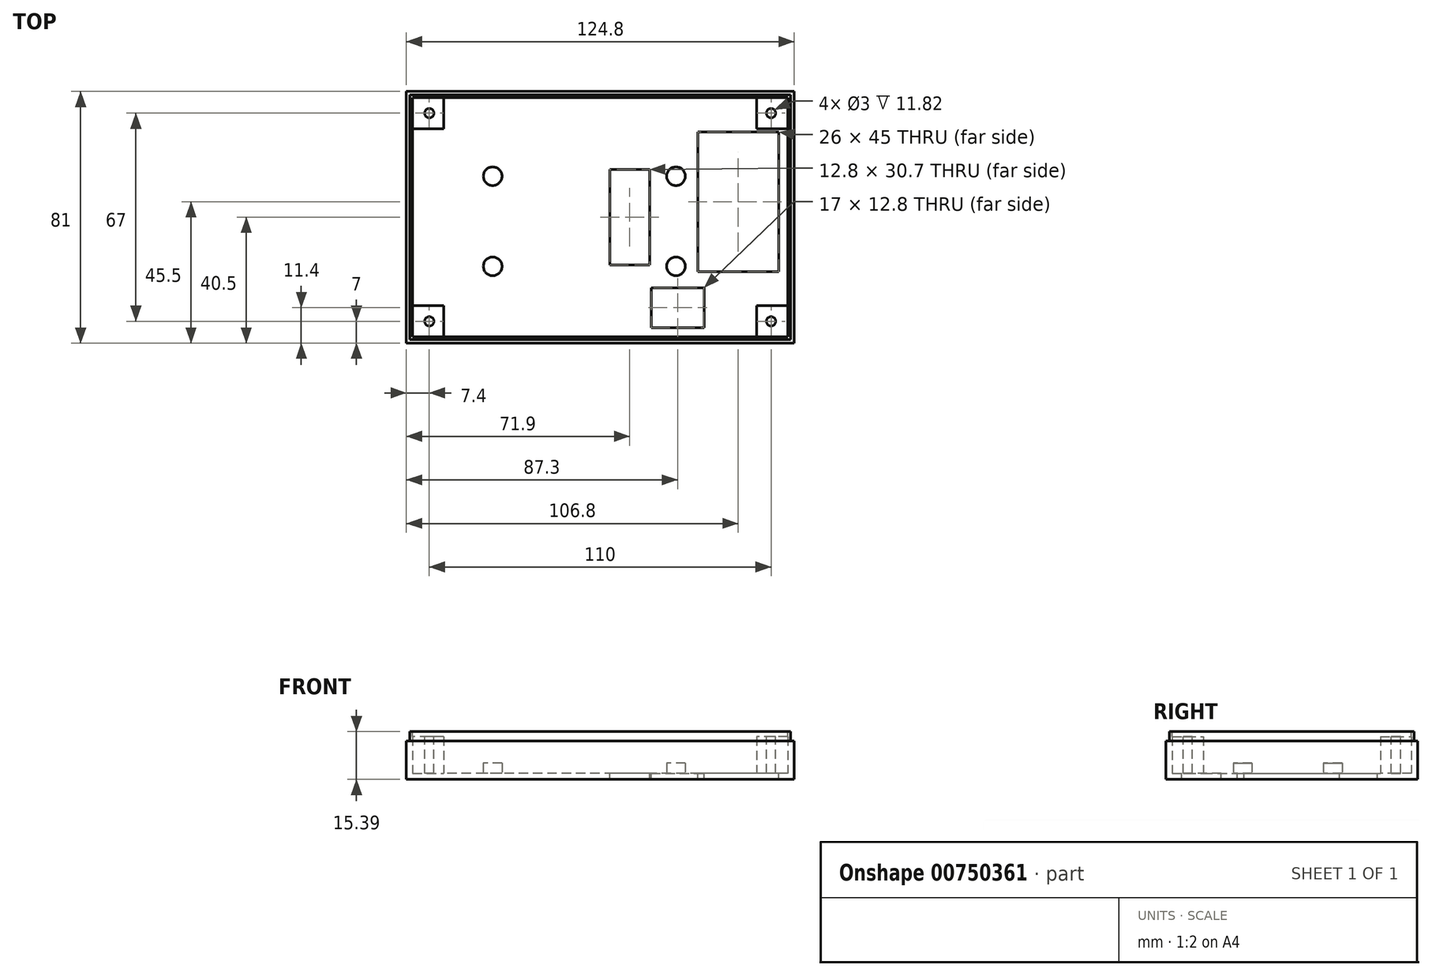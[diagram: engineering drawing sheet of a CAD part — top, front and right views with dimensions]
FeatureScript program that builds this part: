
annotation { "Feature Type Name" : "Feature", "Feature Type Description" : "" }
export const myFeature = defineFeature(function(context is Context, id is Id, definition is map)
    precondition{}
    {
        {
            var Q0;
            Q0=qCreatedBy(makeId("Top.planeOp"),FACE);
            var sketch = newSketch(context, id + "F0", { "sketchPlane" : qUnion([Q0])});
            skLineSegment(sketch, "E0.bottom", {"start": v(-62.4, -40.5) * mm, "end": v(62.4, -40.5) * mm});
            skLineSegment(sketch, "E0.top", {"start": v(-62.4, 40.5) * mm, "end": v(62.4, 40.5) * mm});
            skLineSegment(sketch, "E0.left", {"start": v(-62.4, -40.5) * mm, "end": v(-62.4, 40.5) * mm});
            skLineSegment(sketch, "E0.right", {"start": v(62.4, -40.5) * mm, "end": v(62.4, 40.5) * mm});
            skPoint(sketch, "E0.middle", {"position": v(0, 0) * mm});
            skSolve(sketch);
        }
        {
            var Q0;
            Q0=makeQuery(id+"F0.imprint","IMPRINT",FACE,{"disambiguationData":[TD([[makeQuery(id+"F0.imprint","IMPRINT",EDGE,{"derivedFrom":sQuery(id+"F0.wireOp",EDGE,"E0.bottom")}),1.0]])]});
            extrude(context, id + "F1", {"entities" : qUnion([Q0]), "depth" : 15.4 * mm, "offsetDistance" : 25 * mm});
        }
        {
            var Q0;
            Q0=makeQuery(id+"F1.opExtrude","CAP_FACE",FACE,{"disambiguationData":[OSD([sQuery(id+"F0.wireOp",EDGE,"E0.bottom"),sQuery(id+"F0.wireOp",EDGE,"E0.top"),sQuery(id+"F0.wireOp",EDGE,"E0.left"),sQuery(id+"F0.wireOp",EDGE,"E0.right")])],"isStart":false});
            var sketch = newSketch(context, id + "F2", { "sketchPlane" : qUnion([Q0])});
            skLineSegment(sketch, "E1.bottom", {"start": v(60.4, -38.5) * mm, "end": v(-60.4, -38.5) * mm});
            skLineSegment(sketch, "E1.top", {"start": v(60.4, 38.5) * mm, "end": v(-60.4, 38.5) * mm});
            skLineSegment(sketch, "E1.left", {"start": v(60.4, -38.5) * mm, "end": v(60.4, 38.5) * mm});
            skLineSegment(sketch, "E1.right", {"start": v(-60.4, -38.5) * mm, "end": v(-60.4, 38.5) * mm});
            skPoint(sketch, "E1.middle", {"position": v(0, 0) * mm});
            skSolve(sketch);
        }
        {
            var Q0;
            Q0=makeQuery(id+"F2.imprint","IMPRINT",FACE,{"disambiguationData":[TD([[makeQuery(id+"F2.imprint","IMPRINT",EDGE,{"derivedFrom":sQuery(id+"F2.wireOp",EDGE,"E1.bottom")}),-1.0]])]});
            extrude(context, id + "F3", {"entities" : qUnion([Q0]), "operationType" : NewBodyOperationType.REMOVE, "oppositeDirection" : true, "depth" : 13.4 * mm, "offsetDistance" : 25 * mm});
        }
        {
            var Q0;
            Q0=makeQuery(id+"F1.opExtrude","SWEPT_FACE",FACE,{"disambiguationData":[OSD([sQuery(id+"F0.wireOp",EDGE,"E0.top")])]});
            var sketch = newSketch(context, id + "F4", { "sketchPlane" : qUnion([Q0])});
            skLineSegment(sketch, "E2.bottom", {"start": v(-62.4, 15.4) * mm, "end": v(62.4, 15.4) * mm});
            skLineSegment(sketch, "E2.top", {"start": v(-62.4, 12.4) * mm, "end": v(62.4, 12.4) * mm});
            skLineSegment(sketch, "E2.left", {"start": v(-62.4, 15.4) * mm, "end": v(-62.4, 12.4) * mm});
            skLineSegment(sketch, "E2.right", {"start": v(62.4, 15.4) * mm, "end": v(62.4, 12.4) * mm});
            skSolve(sketch);
        }
        {
            var Q0;
            Q0=makeQuery(id+"F4.imprint","IMPRINT",FACE,{"disambiguationData":[TD([[makeQuery(id+"F4.imprint","IMPRINT",EDGE,{"derivedFrom":sQuery(id+"F4.wireOp",EDGE,"E2.bottom")}),1.0]])]});
            extrude(context, id + "F5", {"entities" : qUnion([Q0]), "operationType" : NewBodyOperationType.REMOVE, "oppositeDirection" : true, "depth" : 1.15 * mm, "offsetDistance" : 25 * mm});
        }
        {
            var Q0;
            Q0=makeQuery(id+"F1.opExtrude","SWEPT_FACE",FACE,{"disambiguationData":[OSD([sQuery(id+"F0.wireOp",EDGE,"E0.bottom")])]});
            var sketch = newSketch(context, id + "F6", { "sketchPlane" : qUnion([Q0])});
            skLineSegment(sketch, "E3.bottom", {"start": v(-62.4, 15.4) * mm, "end": v(62.4, 15.4) * mm});
            skLineSegment(sketch, "E3.top", {"start": v(-62.4, 12.4) * mm, "end": v(62.4, 12.4) * mm});
            skLineSegment(sketch, "E3.left", {"start": v(-62.4, 15.4) * mm, "end": v(-62.4, 12.4) * mm});
            skLineSegment(sketch, "E3.right", {"start": v(62.4, 15.4) * mm, "end": v(62.4, 12.4) * mm});
            skSolve(sketch);
        }
        {
            var Q0;
            Q0=makeQuery(id+"F6.imprint","IMPRINT",FACE,{"disambiguationData":[TD([[makeQuery(id+"F6.imprint","IMPRINT",EDGE,{"derivedFrom":sQuery(id+"F6.wireOp",EDGE,"E3.bottom")}),-1.0]])]});
            extrude(context, id + "F7", {"entities" : qUnion([Q0]), "operationType" : NewBodyOperationType.REMOVE, "oppositeDirection" : true, "depth" : 1.15 * mm, "offsetDistance" : 25 * mm});
        }
        {
            var Q0;
            Q0=makeQuery(id+"F1.opExtrude","SWEPT_FACE",FACE,{"disambiguationData":[OSD([sQuery(id+"F0.wireOp",EDGE,"E0.right")])]});
            var sketch = newSketch(context, id + "F8", { "sketchPlane" : qUnion([Q0])});
            skLineSegment(sketch, "E4.bottom", {"start": v(-39.35, 15.4) * mm, "end": v(39.35, 15.4) * mm});
            skLineSegment(sketch, "E4.top", {"start": v(-39.35, 12.4) * mm, "end": v(39.35, 12.4) * mm});
            skLineSegment(sketch, "E4.left", {"start": v(-39.35, 15.4) * mm, "end": v(-39.35, 12.4) * mm});
            skLineSegment(sketch, "E4.right", {"start": v(39.35, 15.4) * mm, "end": v(39.35, 12.4) * mm});
            skSolve(sketch);
        }
        {
            var Q0;
            Q0=makeQuery(id+"F8.imprint","IMPRINT",FACE,{"disambiguationData":[TD([[makeQuery(id+"F8.imprint","IMPRINT",EDGE,{"derivedFrom":sQuery(id+"F8.wireOp",EDGE,"E4.bottom")}),-1.0]])]});
            extrude(context, id + "F9", {"entities" : qUnion([Q0]), "operationType" : NewBodyOperationType.REMOVE, "oppositeDirection" : true, "depth" : 1.15 * mm, "offsetDistance" : 25 * mm});
        }
        {
            var Q0;
            Q0=makeQuery(id+"F1.opExtrude","SWEPT_FACE",FACE,{"disambiguationData":[OSD([sQuery(id+"F0.wireOp",EDGE,"E0.left")])]});
            var sketch = newSketch(context, id + "F10", { "sketchPlane" : qUnion([Q0])});
            skLineSegment(sketch, "E5.bottom", {"start": v(-39.35, 15.4) * mm, "end": v(39.35, 15.4) * mm});
            skLineSegment(sketch, "E5.top", {"start": v(-39.35, 12.4) * mm, "end": v(39.35, 12.4) * mm});
            skLineSegment(sketch, "E5.left", {"start": v(-39.35, 15.4) * mm, "end": v(-39.35, 12.4) * mm});
            skLineSegment(sketch, "E5.right", {"start": v(39.35, 15.4) * mm, "end": v(39.35, 12.4) * mm});
            skSolve(sketch);
        }
        {
            var Q0;
            Q0=makeQuery(id+"F10.imprint","IMPRINT",FACE,{"disambiguationData":[TD([[makeQuery(id+"F10.imprint","IMPRINT",EDGE,{"derivedFrom":sQuery(id+"F10.wireOp",EDGE,"E5.bottom")}),1.0]])]});
            extrude(context, id + "F11", {"entities" : qUnion([Q0]), "operationType" : NewBodyOperationType.REMOVE, "oppositeDirection" : true, "depth" : 1.15 * mm, "offsetDistance" : 25 * mm});
        }
        {
            var Q0;
            Q0=makeQuery(id+"F3.boolean.opBoolean","COPY",FACE,{"derivedFrom":makeQuery(id+"F3.opExtrude","CAP_FACE",FACE,{"disambiguationData":[OSD([sQuery(id+"F2.wireOp",EDGE,"E1.bottom"),sQuery(id+"F2.wireOp",EDGE,"E1.top"),sQuery(id+"F2.wireOp",EDGE,"E1.left"),sQuery(id+"F2.wireOp",EDGE,"E1.right")])],"isStart":false})});
            var sketch = newSketch(context, id + "F12", { "sketchPlane" : qUnion([Q0])});
            skLineSegment(sketch, "E6.bottom", {"start": v(-60.4, 38.5) * mm, "end": v(-50.4, 38.5) * mm});
            skLineSegment(sketch, "E6.top", {"start": v(-60.4, 28.5) * mm, "end": v(-50.4, 28.5) * mm});
            skLineSegment(sketch, "E6.left", {"start": v(-60.4, 38.5) * mm, "end": v(-60.4, 28.5) * mm});
            skLineSegment(sketch, "E6.right", {"start": v(-50.4, 38.5) * mm, "end": v(-50.4, 28.5) * mm});
            skSolve(sketch);
        }
        {
            var Q0;
            Q0=makeQuery(id+"F12.imprint","IMPRINT",FACE,{"disambiguationData":[TD([[makeQuery(id+"F12.imprint","IMPRINT",EDGE,{"derivedFrom":sQuery(id+"F12.wireOp",EDGE,"E6.bottom")}),1.0]])]});
            extrude(context, id + "F13", {"entities" : qUnion([Q0]), "operationType" : NewBodyOperationType.ADD, "depth" : 11.82 * mm, "offsetDistance" : 25 * mm});
        }
        {
            var Q0;
            Q0=makeQuery(id+"F3.boolean.opBoolean","COPY",FACE,{"derivedFrom":makeQuery(id+"F3.opExtrude","CAP_FACE",FACE,{"disambiguationData":[OSD([sQuery(id+"F2.wireOp",EDGE,"E1.bottom"),sQuery(id+"F2.wireOp",EDGE,"E1.top"),sQuery(id+"F2.wireOp",EDGE,"E1.left"),sQuery(id+"F2.wireOp",EDGE,"E1.right")])],"isStart":false})});
            var sketch = newSketch(context, id + "F14", { "sketchPlane" : qUnion([Q0])});
            skLineSegment(sketch, "E7.bottom", {"start": v(-60.4, -38.5) * mm, "end": v(-50.4, -38.5) * mm});
            skLineSegment(sketch, "E7.top", {"start": v(-60.4, -28.5) * mm, "end": v(-50.4, -28.5) * mm});
            skLineSegment(sketch, "E7.left", {"start": v(-60.4, -38.5) * mm, "end": v(-60.4, -28.5) * mm});
            skLineSegment(sketch, "E7.right", {"start": v(-50.4, -38.5) * mm, "end": v(-50.4, -28.5) * mm});
            skSolve(sketch);
        }
        {
            var Q0;
            Q0=makeQuery(id+"F14.imprint","IMPRINT",FACE,{"disambiguationData":[TD([[makeQuery(id+"F14.imprint","IMPRINT",EDGE,{"derivedFrom":sQuery(id+"F14.wireOp",EDGE,"E7.bottom")}),-1.0]])]});
            extrude(context, id + "F15", {"entities" : qUnion([Q0]), "operationType" : NewBodyOperationType.ADD, "depth" : 11.82 * mm, "offsetDistance" : 25 * mm});
        }
        {
            var Q0;
            Q0=makeQuery(id+"F3.boolean.opBoolean","COPY",FACE,{"derivedFrom":makeQuery(id+"F3.opExtrude","CAP_FACE",FACE,{"disambiguationData":[OSD([sQuery(id+"F2.wireOp",EDGE,"E1.bottom"),sQuery(id+"F2.wireOp",EDGE,"E1.top"),sQuery(id+"F2.wireOp",EDGE,"E1.left"),sQuery(id+"F2.wireOp",EDGE,"E1.right")])],"isStart":false})});
            var sketch = newSketch(context, id + "F16", { "sketchPlane" : qUnion([Q0])});
            skLineSegment(sketch, "E8.bottom", {"start": v(60.4, -38.5) * mm, "end": v(50.4, -38.5) * mm});
            skLineSegment(sketch, "E8.top", {"start": v(60.4, -28.5) * mm, "end": v(50.4, -28.5) * mm});
            skLineSegment(sketch, "E8.left", {"start": v(60.4, -38.5) * mm, "end": v(60.4, -28.5) * mm});
            skLineSegment(sketch, "E8.right", {"start": v(50.4, -38.5) * mm, "end": v(50.4, -28.5) * mm});
            skSolve(sketch);
        }
        {
            var Q0;
            Q0=makeQuery(id+"F16.imprint","IMPRINT",FACE,{"disambiguationData":[TD([[makeQuery(id+"F16.imprint","IMPRINT",EDGE,{"derivedFrom":sQuery(id+"F16.wireOp",EDGE,"E8.bottom")}),-1.0]])]});
            extrude(context, id + "F17", {"entities" : qUnion([Q0]), "operationType" : NewBodyOperationType.ADD, "depth" : 11.82 * mm, "offsetDistance" : 25 * mm});
        }
        {
            var Q0;
            Q0=makeQuery(id+"F3.boolean.opBoolean","COPY",FACE,{"derivedFrom":makeQuery(id+"F3.opExtrude","CAP_FACE",FACE,{"disambiguationData":[OSD([sQuery(id+"F2.wireOp",EDGE,"E1.bottom"),sQuery(id+"F2.wireOp",EDGE,"E1.top"),sQuery(id+"F2.wireOp",EDGE,"E1.left"),sQuery(id+"F2.wireOp",EDGE,"E1.right")])],"isStart":false})});
            var sketch = newSketch(context, id + "F18", { "sketchPlane" : qUnion([Q0])});
            skLineSegment(sketch, "E9.bottom", {"start": v(60.4, 38.5) * mm, "end": v(50.4, 38.5) * mm});
            skLineSegment(sketch, "E9.top", {"start": v(60.4, 28.5) * mm, "end": v(50.4, 28.5) * mm});
            skLineSegment(sketch, "E9.left", {"start": v(60.4, 38.5) * mm, "end": v(60.4, 28.5) * mm});
            skLineSegment(sketch, "E9.right", {"start": v(50.4, 38.5) * mm, "end": v(50.4, 28.5) * mm});
            skSolve(sketch);
        }
        {
            var Q0;
            Q0=makeQuery(id+"F18.imprint","IMPRINT",FACE,{"disambiguationData":[TD([[makeQuery(id+"F18.imprint","IMPRINT",EDGE,{"derivedFrom":sQuery(id+"F18.wireOp",EDGE,"E9.bottom")}),1.0]])]});
            extrude(context, id + "F19", {"entities" : qUnion([Q0]), "operationType" : NewBodyOperationType.ADD, "depth" : 11.82 * mm, "offsetDistance" : 25 * mm});
        }
        {
            var Q0;
            Q0=makeQuery(id+"F13.opExtrude","CAP_FACE",FACE,{"disambiguationData":[OSD([sQuery(id+"F12.wireOp",EDGE,"E6.bottom"),sQuery(id+"F12.wireOp",EDGE,"E6.top"),sQuery(id+"F12.wireOp",EDGE,"E6.left"),sQuery(id+"F12.wireOp",EDGE,"E6.right")])],"isStart":false});
            var sketch = newSketch(context, id + "F20", { "sketchPlane" : qUnion([Q0])});
            skCircle(sketch, "E10", {"center": v(-55, 33.5) * mm, "radius": 1.5 * mm});
            skSolve(sketch);
        }
        {
            var Q0;
            Q0=makeQuery(id+"F20.imprint","IMPRINT",FACE,{"disambiguationData":[TD([[makeQuery(id+"F20.imprint","IMPRINT",EDGE,{"derivedFrom":sQuery(id+"F20.wireOp",EDGE,"E10")}),1.0]])]});
            var Q1;
            Q1=qSketchRegion(id+"F20",true);
            extrude(context, id + "F21", {"entities" : qUnion([Q0, Q1]), "operationType" : NewBodyOperationType.REMOVE, "oppositeDirection" : true, "depth" : 11.82 * mm, "offsetDistance" : 25 * mm});
        }
        {
            var Q0;
            Q0=makeQuery(id+"F15.opExtrude","CAP_FACE",FACE,{"disambiguationData":[OSD([sQuery(id+"F14.wireOp",EDGE,"E7.bottom"),sQuery(id+"F14.wireOp",EDGE,"E7.top"),sQuery(id+"F14.wireOp",EDGE,"E7.left"),sQuery(id+"F14.wireOp",EDGE,"E7.right")])],"isStart":false});
            var sketch = newSketch(context, id + "F22", { "sketchPlane" : qUnion([Q0])});
            skCircle(sketch, "E11", {"center": v(-55, -33.5) * mm, "radius": 1.5 * mm});
            skSolve(sketch);
        }
        {
            var Q0;
            Q0=makeQuery(id+"F22.imprint","IMPRINT",FACE,{"disambiguationData":[TD([[makeQuery(id+"F22.imprint","IMPRINT",EDGE,{"derivedFrom":sQuery(id+"F22.wireOp",EDGE,"E11")}),1.0]])]});
            extrude(context, id + "F23", {"entities" : qUnion([Q0]), "operationType" : NewBodyOperationType.REMOVE, "oppositeDirection" : true, "depth" : 11.82 * mm, "offsetDistance" : 25 * mm});
        }
        {
            var Q0;
            Q0=makeQuery(id+"F17.opExtrude","CAP_FACE",FACE,{"disambiguationData":[OSD([sQuery(id+"F16.wireOp",EDGE,"E8.bottom"),sQuery(id+"F16.wireOp",EDGE,"E8.top"),sQuery(id+"F16.wireOp",EDGE,"E8.left"),sQuery(id+"F16.wireOp",EDGE,"E8.right")])],"isStart":false});
            var sketch = newSketch(context, id + "F24", { "sketchPlane" : qUnion([Q0])});
            skCircle(sketch, "E12", {"center": v(55, -33.5) * mm, "radius": 1.5 * mm});
            skSolve(sketch);
        }
        {
            var Q0;
            Q0=makeQuery(id+"F24.imprint","IMPRINT",FACE,{"disambiguationData":[TD([[makeQuery(id+"F24.imprint","IMPRINT",EDGE,{"derivedFrom":sQuery(id+"F24.wireOp",EDGE,"E12")}),1.0]])]});
            extrude(context, id + "F25", {"entities" : qUnion([Q0]), "operationType" : NewBodyOperationType.REMOVE, "oppositeDirection" : true, "depth" : 11.82 * mm, "offsetDistance" : 25 * mm});
        }
        {
            var Q0;
            Q0=makeQuery(id+"F19.opExtrude","CAP_FACE",FACE,{"disambiguationData":[OSD([sQuery(id+"F18.wireOp",EDGE,"E9.bottom"),sQuery(id+"F18.wireOp",EDGE,"E9.top"),sQuery(id+"F18.wireOp",EDGE,"E9.left"),sQuery(id+"F18.wireOp",EDGE,"E9.right")])],"isStart":false});
            var sketch = newSketch(context, id + "F26", { "sketchPlane" : qUnion([Q0])});
            skCircle(sketch, "E13", {"center": v(55, 33.5) * mm, "radius": 1.5 * mm});
            skSolve(sketch);
        }
        {
            var Q0;
            Q0=makeQuery(id+"F26.imprint","IMPRINT",FACE,{"disambiguationData":[TD([[makeQuery(id+"F26.imprint","IMPRINT",EDGE,{"derivedFrom":sQuery(id+"F26.wireOp",EDGE,"E13")}),1.0]])]});
            extrude(context, id + "F27", {"entities" : qUnion([Q0]), "operationType" : NewBodyOperationType.REMOVE, "oppositeDirection" : true, "depth" : 11.82 * mm, "offsetDistance" : 25 * mm});
        }
        {
            var Q0;
            Q0=makeQuery(id+"F3.boolean.opBoolean","COPY",FACE,{"derivedFrom":makeQuery(id+"F3.opExtrude","CAP_FACE",FACE,{"disambiguationData":[OSD([sQuery(id+"F2.wireOp",EDGE,"E1.bottom"),sQuery(id+"F2.wireOp",EDGE,"E1.top"),sQuery(id+"F2.wireOp",EDGE,"E1.left"),sQuery(id+"F2.wireOp",EDGE,"E1.right")])],"isStart":false})});
            var sketch = newSketch(context, id + "F28", { "sketchPlane" : qUnion([Q0])});
            skLineSegment(sketch, "E14.bottom", {"start": v(57.4, -17.5) * mm, "end": v(31.4, -17.5) * mm});
            skLineSegment(sketch, "E14.top", {"start": v(57.4, 27.5) * mm, "end": v(31.4, 27.5) * mm});
            skLineSegment(sketch, "E14.left", {"start": v(57.4, -17.5) * mm, "end": v(57.4, 27.5) * mm});
            skLineSegment(sketch, "E14.right", {"start": v(31.4, -17.5) * mm, "end": v(31.4, 27.5) * mm});
            skPoint(sketch, "E14.middle", {"position": v(44.4, 5) * mm});
            skSolve(sketch);
        }
        {
            var Q0;
            Q0 = qSketchRegion(id + "F28", true);
            extrude(context, id + "F29", {"entities" : qUnion([Q0]), "operationType" : NewBodyOperationType.REMOVE, "endBound" : BoundingType.THROUGH_ALL, "oppositeDirection" : true, "depth" : 25 * mm, "offsetDistance" : 25 * mm});
        }
        {
            var Q0;
            Q0=makeQuery(id+"F3.boolean.opBoolean","COPY",FACE,{"derivedFrom":makeQuery(id+"F3.opExtrude","CAP_FACE",FACE,{"disambiguationData":[OSD([sQuery(id+"F2.wireOp",EDGE,"E1.bottom"),sQuery(id+"F2.wireOp",EDGE,"E1.top"),sQuery(id+"F2.wireOp",EDGE,"E1.left"),sQuery(id+"F2.wireOp",EDGE,"E1.right")])],"isStart":false})});
            var sketch = newSketch(context, id + "F30", { "sketchPlane" : qUnion([Q0])});
            skLineSegment(sketch, "E15.bottom", {"start": v(15.9, -15.35) * mm, "end": v(3.1, -15.35) * mm});
            skLineSegment(sketch, "E15.top", {"start": v(15.9, 15.35) * mm, "end": v(3.1, 15.35) * mm});
            skLineSegment(sketch, "E15.left", {"start": v(15.9, -15.35) * mm, "end": v(15.9, 15.35) * mm});
            skLineSegment(sketch, "E15.right", {"start": v(3.1, -15.35) * mm, "end": v(3.1, 15.35) * mm});
            skPoint(sketch, "E15.middle", {"position": v(9.5, 0) * mm});
            skSolve(sketch);
        }
        {
            var Q0;
            Q0 = qSketchRegion(id + "F30", true);
            extrude(context, id + "F31", {"entities" : qUnion([Q0]), "operationType" : NewBodyOperationType.REMOVE, "endBound" : BoundingType.THROUGH_ALL, "oppositeDirection" : true, "depth" : 25 * mm, "offsetDistance" : 25 * mm});
        }
        {
            var Q0;
            Q0=makeQuery(id+"F3.boolean.opBoolean","COPY",FACE,{"derivedFrom":makeQuery(id+"F3.opExtrude","CAP_FACE",FACE,{"disambiguationData":[OSD([sQuery(id+"F2.wireOp",EDGE,"E1.bottom"),sQuery(id+"F2.wireOp",EDGE,"E1.top"),sQuery(id+"F2.wireOp",EDGE,"E1.left"),sQuery(id+"F2.wireOp",EDGE,"E1.right")])],"isStart":false})});
            var sketch = newSketch(context, id + "F32", { "sketchPlane" : qUnion([Q0])});
            skLineSegment(sketch, "E16.bottom", {"start": v(16.4, -22.7) * mm, "end": v(33.4, -22.7) * mm});
            skLineSegment(sketch, "E16.top", {"start": v(16.4, -35.5) * mm, "end": v(33.4, -35.5) * mm});
            skLineSegment(sketch, "E16.left", {"start": v(16.4, -22.7) * mm, "end": v(16.4, -35.5) * mm});
            skLineSegment(sketch, "E16.right", {"start": v(33.4, -22.7) * mm, "end": v(33.4, -35.5) * mm});
            skSolve(sketch);
        }
        {
            var Q0;
            Q0 = qSketchRegion(id + "F32", true);
            extrude(context, id + "F33", {"entities" : qUnion([Q0]), "operationType" : NewBodyOperationType.REMOVE, "endBound" : BoundingType.THROUGH_ALL, "oppositeDirection" : true, "depth" : 25 * mm, "offsetDistance" : 25 * mm});
        }
        {
            var Q0;
            Q0=makeQuery(id+"F3.boolean.opBoolean","COPY",FACE,{"derivedFrom":makeQuery(id+"F3.opExtrude","CAP_FACE",FACE,{"disambiguationData":[OSD([sQuery(id+"F2.wireOp",EDGE,"E1.bottom"),sQuery(id+"F2.wireOp",EDGE,"E1.top"),sQuery(id+"F2.wireOp",EDGE,"E1.left"),sQuery(id+"F2.wireOp",EDGE,"E1.right")])],"isStart":false})});
            var sketch = newSketch(context, id + "F34", { "sketchPlane" : qUnion([Q0])});
            skCircle(sketch, "E17", {"center": v(24.4, 13.2) * mm, "radius": 3 * mm});
            skCircle(sketch, "E18", {"center": v(24.4, -15.8) * mm, "radius": 3 * mm});
            skCircle(sketch, "E19", {"center": v(-34.6, 13.2) * mm, "radius": 3 * mm});
            skCircle(sketch, "E20", {"center": v(-34.6, -15.8) * mm, "radius": 3 * mm});
            skSolve(sketch);
        }
        {
            var Q0;
            Q0 = qSketchRegion(id + "F34", true);
            extrude(context, id + "F35", {"entities" : qUnion([Q0]), "operationType" : NewBodyOperationType.ADD, "depth" : 3.3 * mm, "offsetDistance" : 25 * mm});
        }
        {
            var Q0;
            Q0=makeQuery(id+"F1.opExtrude","CAP_FACE",FACE,{"disambiguationData":[OSD([sQuery(id+"F0.wireOp",EDGE,"E0.bottom"),sQuery(id+"F0.wireOp",EDGE,"E0.top"),sQuery(id+"F0.wireOp",EDGE,"E0.left"),sQuery(id+"F0.wireOp",EDGE,"E0.right")])],"isStart":true});
            var sketch = newSketch(context, id + "F36", { "sketchPlane" : qUnion([Q0])});
            skSolve(sketch);
        }
        {
            var Q0;
            {var subQ3=sQuery(id+"F0.wireOp",EDGE,"E0.bottom");Q0=makeQuery(id+"F36.imprint","IMPRINT",FACE,{"disambiguationData":[TD([[makeQuery(id+"F36.imprint","IMPRINT",EDGE,{"derivedFrom":makeQuery(id+"F1.opExtrude","CAP_EDGE",EDGE,{"disambiguationData":[OSD([subQ3])],"isStart":true})}),-1.0]])]});}
            var sketch = newSketch(context, id + "F37", { "sketchPlane" : qUnion([Q0])});
            skSolve(sketch);
        }
    });
